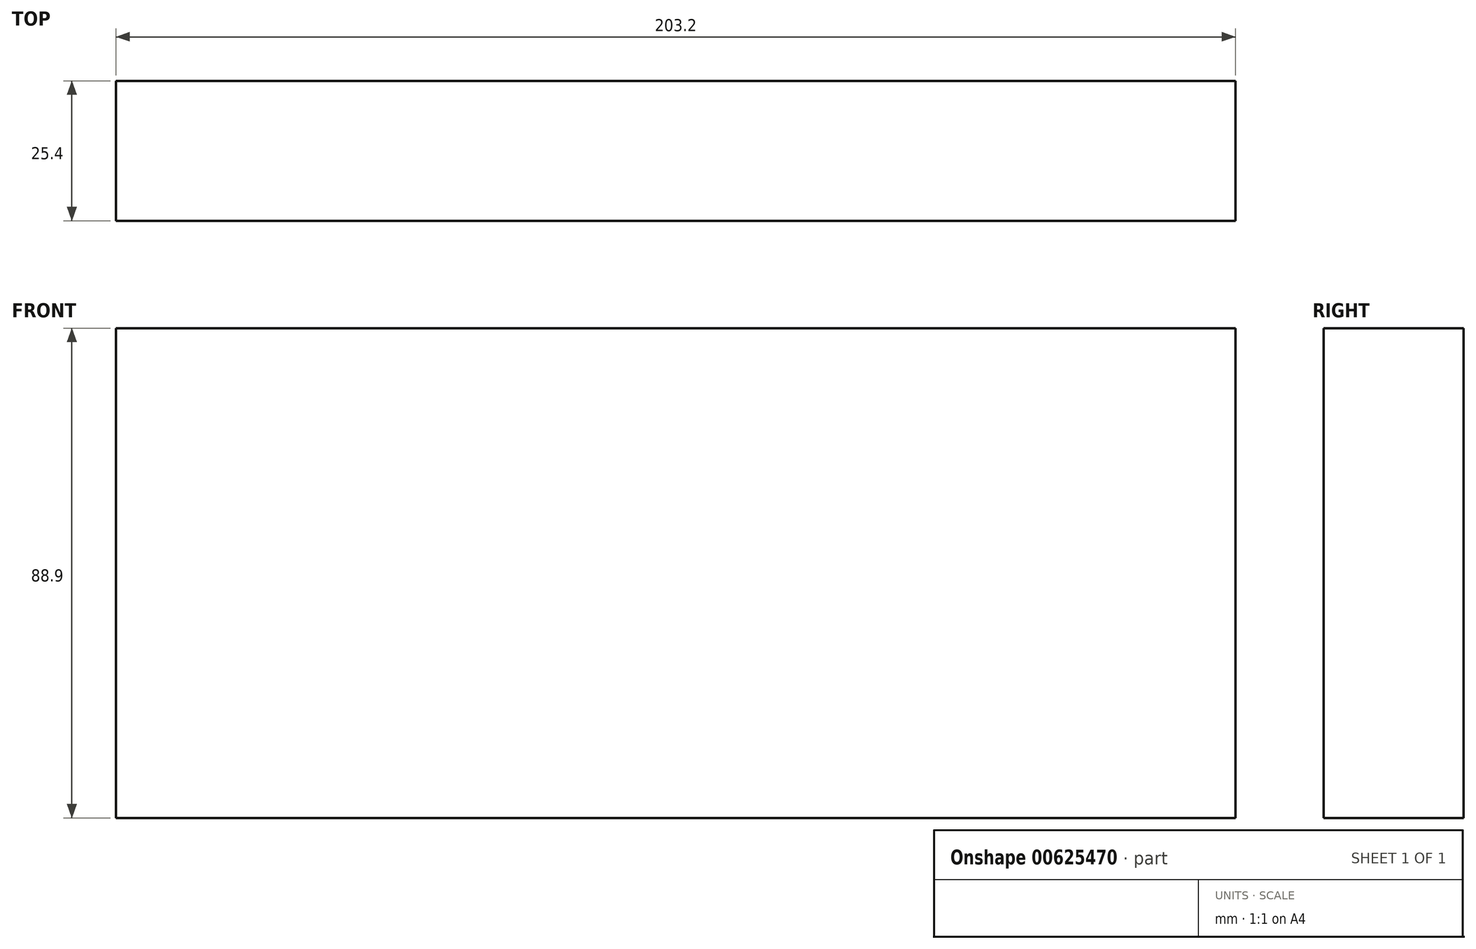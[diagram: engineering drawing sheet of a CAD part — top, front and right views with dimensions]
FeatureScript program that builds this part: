
annotation { "Feature Type Name" : "Feature", "Feature Type Description" : "" }
export const myFeature = defineFeature(function(context is Context, id is Id, definition is map)
    precondition{}
    {
        {
            var Q0;
            Q0=qCreatedBy(makeId("Front.planeOp"),FACE);
            var sketch = newSketch(context, id + "F0", { "sketchPlane" : qUnion([Q0])});
            skLineSegment(sketch, "E0.bottom", {"start": v(0, 0) * mm, "end": v(203.2, 0) * mm});
            skLineSegment(sketch, "E0.top", {"start": v(0, 88.9) * mm, "end": v(203.2, 88.9) * mm});
            skLineSegment(sketch, "E0.left", {"start": v(0, 0) * mm, "end": v(0, 88.9) * mm});
            skLineSegment(sketch, "E0.right", {"start": v(203.2, 0) * mm, "end": v(203.2, 88.9) * mm});
            skLineSegment(sketch, "E1", {"start": v(0, 88.9) * mm, "end": v(101.42, 88.9) * mm});
            skSolve(sketch);
        }
        {
            var Q0;
            Q0 = qSketchRegion(id + "F0", true);
            extrude(context, id + "F1", {"entities" : qUnion([Q0]), "depth" : 25.4 * mm, "offsetDistance" : 25.4 * mm});
        }
    });
